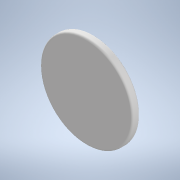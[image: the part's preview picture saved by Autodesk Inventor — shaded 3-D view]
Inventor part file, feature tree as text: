
AUTODESK INVENTOR PART (.ipt)
format: ipt  version: 2020 (Build 240168000, 168)  size: 109,568 bytes
history: native  units: mm
features: extrude x1, fillet x1, sketch x1
ambient origin geometry x8: Origin, YZ Plane, XZ Plane, XY Plane, X Axis, Y Axis, Z Axis, Center Point
bodies: Solid1 (feature_tree)
feature tree (3):
  extrude  "Extrusion1"  Depth=2.0mm TaperAngle=0.0deg
  fillet  "Fillet1"  Radius=0.5mm
  sketch  "Sketch1"  dims[d0=25.0mm d1=2.0mm d2=0.0mm d3=0.5mm]
